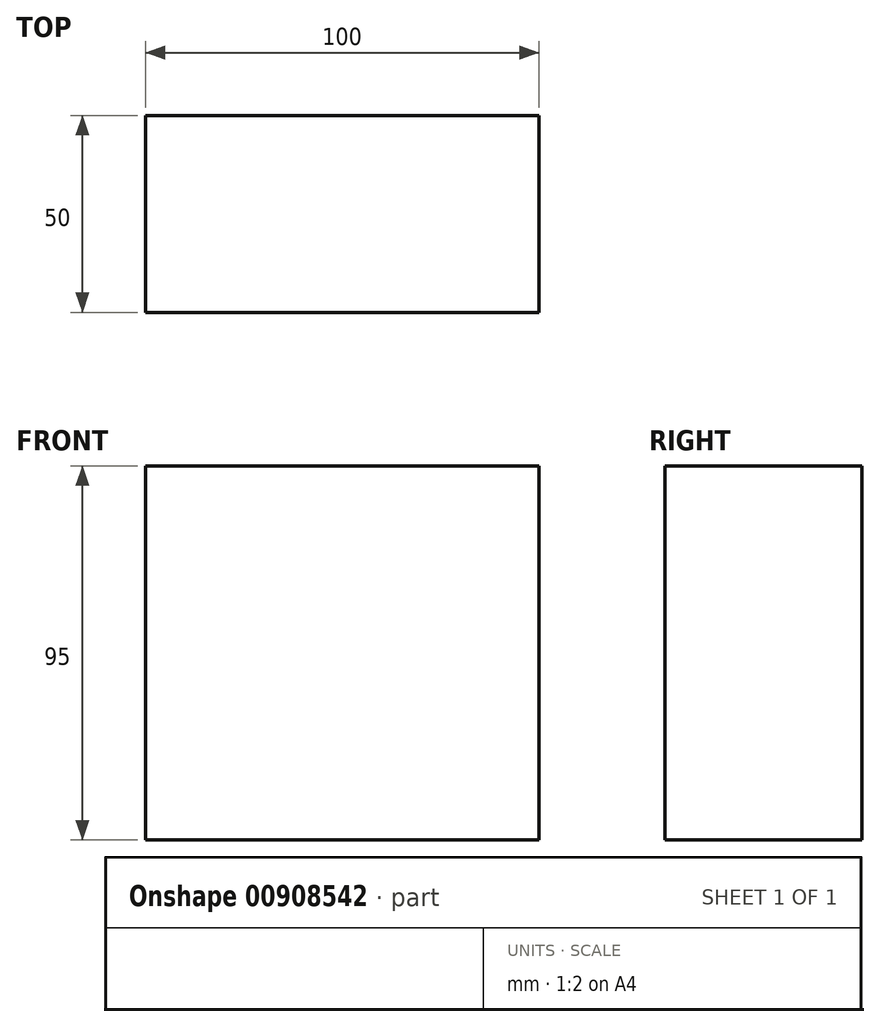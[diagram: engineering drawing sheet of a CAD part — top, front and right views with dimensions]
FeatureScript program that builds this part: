
annotation { "Feature Type Name" : "Feature", "Feature Type Description" : "" }
export const myFeature = defineFeature(function(context is Context, id is Id, definition is map)
    precondition{}
    {
        {
            var Q0;
            Q0=qCreatedBy(makeId("Front.planeOp"),FACE);
            var sketch = newSketch(context, id + "F0", { "sketchPlane" : qUnion([Q0])});
            skLineSegment(sketch, "E0.bottom", {"start": v(-50, -47.5) * mm, "end": v(50, -47.5) * mm});
            skLineSegment(sketch, "E0.top", {"start": v(-50, 47.5) * mm, "end": v(50, 47.5) * mm});
            skLineSegment(sketch, "E0.left", {"start": v(-50, -47.5) * mm, "end": v(-50, 47.5) * mm});
            skLineSegment(sketch, "E0.right", {"start": v(50, -47.5) * mm, "end": v(50, 47.5) * mm});
            skPoint(sketch, "E0.middle", {"position": v(0, 0) * mm});
            skSolve(sketch);
        }
        {
            var Q0;
            Q0=makeQuery(id+"F0.imprint","IMPRINT",FACE,{"disambiguationData":[TD([[makeQuery(id+"F0.imprint","IMPRINT",EDGE,{"derivedFrom":sQuery(id+"F0.wireOp",EDGE,"E0.bottom")}),1.0]])]});
            extrude(context, id + "F1", {"entities" : qUnion([Q0]), "depth" : 50 * mm, "offsetDistance" : 25 * mm});
        }
    });
